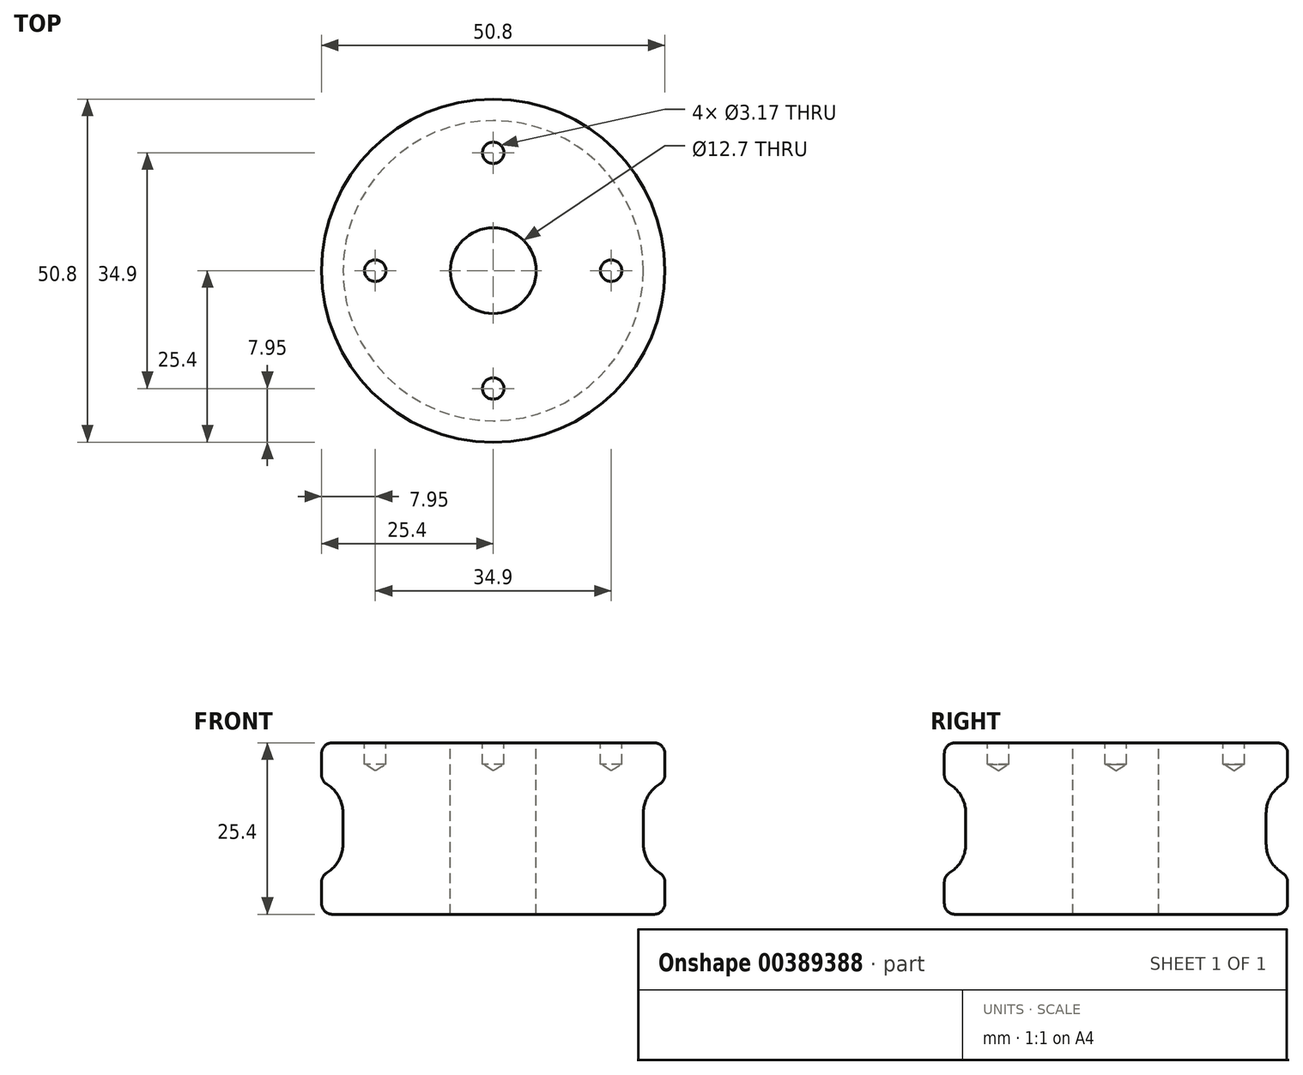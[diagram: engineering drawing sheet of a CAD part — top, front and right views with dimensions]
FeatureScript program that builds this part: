
annotation { "Feature Type Name" : "Feature", "Feature Type Description" : "" }
export const myFeature = defineFeature(function(context is Context, id is Id, definition is map)
    precondition{}
    {
        {
            var Q0;
            Q0=qCreatedBy(makeId("Top.planeOp"),FACE);
            var sketch = newSketch(context, id + "F0", { "sketchPlane" : qUnion([Q0])});
            skCircle(sketch, "E0", {"center": v(0, 0) * mm, "radius": 25.4 * mm});
            skSolve(sketch);
        }
        {
            var Q0;
            Q0 = qSketchRegion(id + "F0", true);
            extrude(context, id + "F1", {"entities" : qUnion([Q0]), "depth" : 6.35 * mm});
        }
        {
            var Q0;
            Q0=makeQuery(id+"F1.opExtrude","CAP_FACE",FACE,{"disambiguationData":[OSD([sQuery(id+"F0.wireOp",EDGE,"E0")])],"isStart":false});
            var sketch = newSketch(context, id + "F2", { "sketchPlane" : qUnion([Q0])});
            skCircle(sketch, "E1", {"center": v(0, 0) * mm, "radius": 22.23 * mm});
            skSolve(sketch);
        }
        {
            var Q0;
            Q0 = qSketchRegion(id + "F2", true);
            extrude(context, id + "F3", {"entities" : qUnion([Q0]), "operationType" : NewBodyOperationType.ADD, "depth" : 12.7 * mm});
        }
        {
            var Q0;
            Q0=makeQuery(id+"F3.opExtrude","CAP_FACE",FACE,{"disambiguationData":[OSD([sQuery(id+"F2.wireOp",EDGE,"E1")])],"isStart":false});
            var sketch = newSketch(context, id + "F4", { "sketchPlane" : qUnion([Q0])});
            skCircle(sketch, "E2", {"center": v(0, 0) * mm, "radius": 25.4 * mm});
            skSolve(sketch);
        }
        {
            var Q0;
            Q0 = qSketchRegion(id + "F4", true);
            extrude(context, id + "F5", {"entities" : qUnion([Q0]), "operationType" : NewBodyOperationType.ADD, "depth" : 6.35 * mm});
        }
        {
            var Q0;
            Q0=makeQuery(id+"F1.opExtrude","CAP_EDGE",EDGE,{"disambiguationData":[OSD([sQuery(id+"F0.wireOp",EDGE,"E0")])],"isStart":false});
            var Q1;
            Q1=makeQuery(id+"F5.opExtrude","CAP_EDGE",EDGE,{"disambiguationData":[OSD([sQuery(id+"F4.wireOp",EDGE,"E2")])],"isStart":true});
            var Q2;
            Q2=makeQuery(id+"F1.opExtrude","SWEPT_FACE",FACE,{"disambiguationData":[OSD([sQuery(id+"F0.wireOp",EDGE,"E0")])]});
            var Q3;
            Q3=makeQuery(id+"F5.opExtrude","CAP_EDGE",EDGE,{"disambiguationData":[OSD([sQuery(id+"F4.wireOp",EDGE,"E2")])],"isStart":false});
            fillet(context, id + "F6", {"entities" : qUnion([Q0, Q1, Q2, Q3]), "radius" : 1.6 * mm, "tangentPropagation" : true, "allowEdgeOverflow" : false});
        }
        {
            var Q0;
            Q0=makeQuery(id+"F3.opExtrude","SWEPT_FACE",FACE,{"disambiguationData":[OSD([sQuery(id+"F2.wireOp",EDGE,"E1")])]});
            fillet(context, id + "F7", {"entities" : qUnion([Q0]), "radius" : 5.08 * mm, "tangentPropagation" : true, "allowEdgeOverflow" : false});
        }
        {
            var Q0;
            Q0=makeQuery(id+"F5.opExtrude","CAP_FACE",FACE,{"disambiguationData":[OSD([sQuery(id+"F4.wireOp",EDGE,"E2")])],"isStart":false});
            var sketch = newSketch(context, id + "F8", { "sketchPlane" : qUnion([Q0])});
            skCircle(sketch, "E3", {"center": v(0, -17.45) * mm, "radius": 1.59 * mm});
            skCircle(sketch, "E4.MirrorC", {"center": v(0, 17.45) * mm, "radius": 1.59 * mm});
            skCircle(sketch, "E5", {"center": v(-17.45, 0) * mm, "radius": 1.59 * mm});
            skCircle(sketch, "E6.MirrorC", {"center": v(17.45, 0) * mm, "radius": 1.59 * mm});
            skCircle(sketch, "E7", {"center": v(0, 0) * mm, "radius": 6.35 * mm});
            skSolve(sketch);
        }
        {
            var Q0;
            Q0=sQuery(id+"F8.wireOp",VERTEX,"E3.center");
            var Q1;
            Q1=sQuery(id+"F8.wireOp",VERTEX,"E5.center");
            var Q2;
            Q2=sQuery(id+"F8.wireOp",VERTEX,"E4.MirrorC.center");
            var Q3;
            Q3=sQuery(id+"F8.wireOp",VERTEX,"E6.MirrorC.center");
            var Q4;
            Q4=makeQuery(id+"F1.opExtrude","SWEPT_BODY",BODY,{"disambiguationData":[OSD([sQuery(id+"F0.wireOp",EDGE,"E0")])]});
            hole(context, id + "F9", {"style" : HoleStyle.C_BORE, "endStyle" : HoleEndStyle.BLIND, "holeDiameter" : 3.17 * mm, "cBoreDiameter" : 3.17 * mm, "cBoreDepth" : 3.17 * mm, "holeDepth" : 3.17 * mm, "isTappedThrough" : true, "tappedDepth" : 12.7 * mm, "tapClearance" : 3, "locations" : qUnion([Q0, Q1, Q2, Q3]), "scope" : qUnion([Q4])});
        }
        {
            var Q0;
            Q0=sQuery(id+"F8.wireOp",VERTEX,"E7.center");
            var Q1;
            Q1=makeQuery(id+"F1.opExtrude","SWEPT_BODY",BODY,{"disambiguationData":[OSD([sQuery(id+"F0.wireOp",EDGE,"E0")])]});
            hole(context, id + "F10", {"style" : HoleStyle.SIMPLE, "endStyle" : HoleEndStyle.THROUGH, "holeDiameter" : 12.7 * mm, "isTappedThrough" : true, "tappedDepth" : 12.7 * mm, "tapClearance" : 3, "locations" : qUnion([Q0]), "scope" : qUnion([Q1])});
        }
    });
